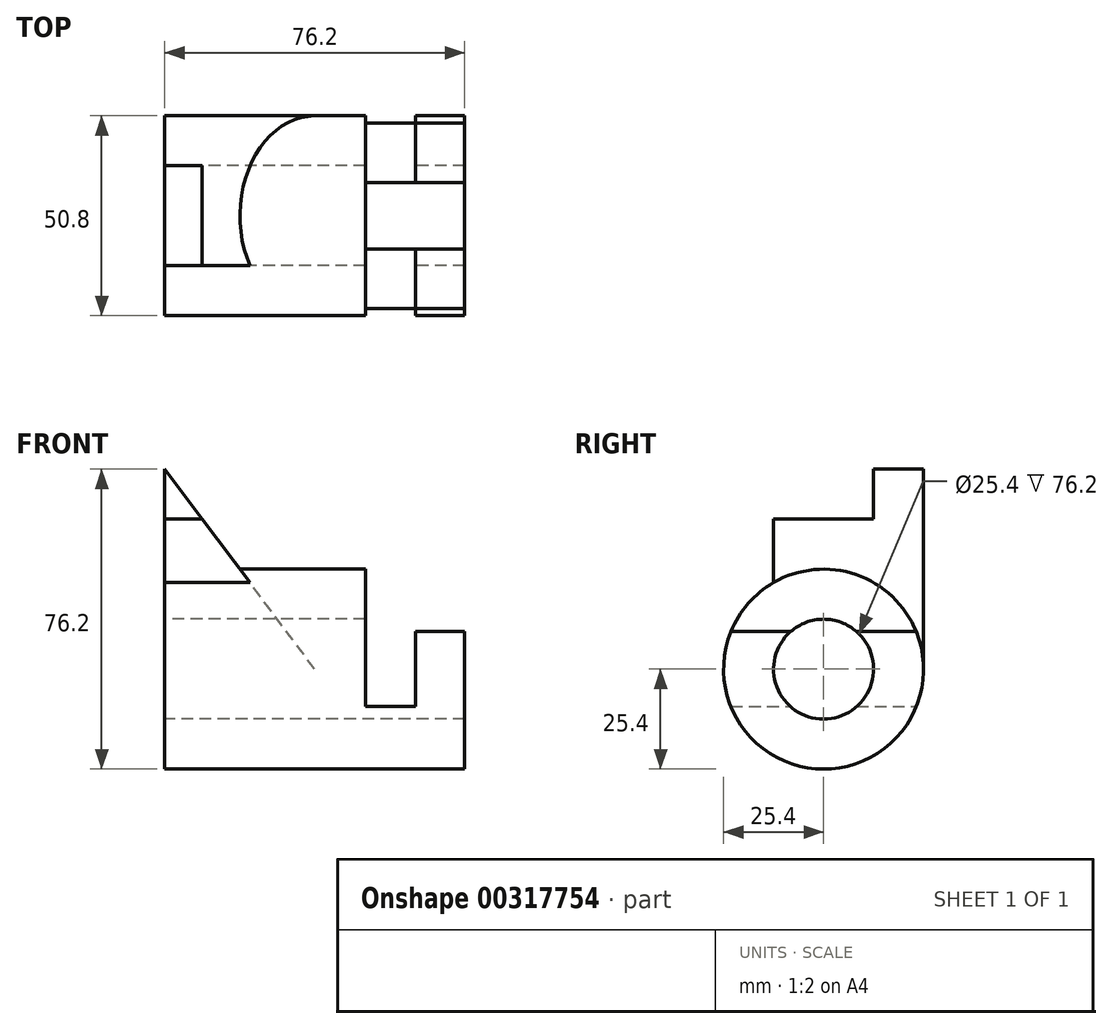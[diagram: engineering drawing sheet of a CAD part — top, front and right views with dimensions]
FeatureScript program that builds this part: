
annotation { "Feature Type Name" : "Feature", "Feature Type Description" : "" }
export const myFeature = defineFeature(function(context is Context, id is Id, definition is map)
    precondition{}
    {
        {
            var Q0;
            Q0=qCreatedBy(makeId("Front.planeOp"),FACE);
            var sketch = newSketch(context, id + "F0", { "sketchPlane" : qUnion([Q0])});
            skLineSegment(sketch, "E0", {"start": v(0, 0) * mm, "end": v(0, 50.8) * mm});
            skLineSegment(sketch, "E1", {"start": v(0, 0) * mm, "end": v(38.1, 0) * mm});
            skLineSegment(sketch, "E2", {"start": v(38.1, 0) * mm, "end": v(0, 50.8) * mm});
            skSolve(sketch);
        }
        {
            var Q0;
            Q0 = qSketchRegion(id + "F0", true);
            extrude(context, id + "F1", {"entities" : qUnion([Q0]), "oppositeDirection" : true, "depth" : 25.4 * mm});
        }
        {
            var Q0;
            Q0=makeQuery(id+"F1.opExtrude","CAP_FACE",FACE,{"disambiguationData":[OSD([sQuery(id+"F0.wireOp",EDGE,"E0"),sQuery(id+"F0.wireOp",EDGE,"E1"),sQuery(id+"F0.wireOp",EDGE,"E2")])],"isStart":true});
            var sketch = newSketch(context, id + "F2", { "sketchPlane" : qUnion([Q0])});
            skLineSegment(sketch, "E3", {"start": v(0, 50.8) * mm, "end": v(0, 0) * mm});
            skLineSegment(sketch, "E4", {"start": v(0, 0) * mm, "end": v(38.1, 0) * mm});
            skLineSegment(sketch, "E5", {"start": v(38.1, 0) * mm, "end": v(0, 50.8) * mm});
            skSolve(sketch);
        }
        {
            var Q0;
            Q0 = qSketchRegion(id + "F2", true);
            extrude(context, id + "F3", {"entities" : qUnion([Q0]), "operationType" : NewBodyOperationType.ADD, "depth" : 12.7 * mm});
        }
        {
            var Q0;
            Q0=makeQuery(id+"F3.boolean.opBoolean","MERGE",FACE,{"derivedFrom":[makeQuery(id+"F1.opExtrude","SWEPT_FACE",FACE,{"disambiguationData":[OSD([sQuery(id+"F0.wireOp",EDGE,"E0")])]}),makeQuery(id+"F3.opExtrude","SWEPT_FACE",FACE,{"disambiguationData":[OSD([sQuery(id+"F2.wireOp",EDGE,"E3")])]})]});
            var sketch = newSketch(context, id + "F4", { "sketchPlane" : qUnion([Q0])});
            skCircle(sketch, "E6", {"center": v(0, 0) * mm, "radius": 25.4 * mm});
            skSolve(sketch);
        }
        {
            var Q0;
            Q0 = qSketchRegion(id + "F4", true);
            extrude(context, id + "F5", {"entities" : qUnion([Q0]), "operationType" : NewBodyOperationType.ADD, "oppositeDirection" : true, "depth" : 76.2 * mm});
        }
        {
            var Q0;
            Q0=makeQuery(id+"F5.boolean.opBoolean","MERGE",FACE,{"derivedFrom":[makeQuery(id+"F3.boolean.opBoolean","MERGE",FACE,{"derivedFrom":[makeQuery(id+"F1.opExtrude","SWEPT_FACE",FACE,{"disambiguationData":[OSD([sQuery(id+"F0.wireOp",EDGE,"E0")])]}),makeQuery(id+"F3.opExtrude","SWEPT_FACE",FACE,{"disambiguationData":[OSD([sQuery(id+"F2.wireOp",EDGE,"E3")])]})]}),makeQuery(id+"F5.opExtrude","CAP_FACE",FACE,{"disambiguationData":[OSD([sQuery(id+"F4.wireOp",EDGE,"E6")])],"isStart":true})]});
            var sketch = newSketch(context, id + "F6", { "sketchPlane" : qUnion([Q0])});
            skCircle(sketch, "E7", {"center": v(0, 0) * mm, "radius": 12.7 * mm});
            skSolve(sketch);
        }
        {
            var Q0;
            Q0 = qSketchRegion(id + "F6", true);
            extrude(context, id + "F7", {"entities" : qUnion([Q0]), "operationType" : NewBodyOperationType.REMOVE, "endBound" : BoundingType.THROUGH_ALL, "oppositeDirection" : true, "depth" : 25.4 * mm});
        }
        {
            var Q0;
            Q0=makeQuery(id+"F5.boolean.opBoolean","MERGE",FACE,{"derivedFrom":[makeQuery(id+"F3.boolean.opBoolean","MERGE",FACE,{"derivedFrom":[makeQuery(id+"F1.opExtrude","SWEPT_FACE",FACE,{"disambiguationData":[OSD([sQuery(id+"F0.wireOp",EDGE,"E0")])]}),makeQuery(id+"F3.opExtrude","SWEPT_FACE",FACE,{"disambiguationData":[OSD([sQuery(id+"F2.wireOp",EDGE,"E3")])]})]}),makeQuery(id+"F5.opExtrude","CAP_FACE",FACE,{"disambiguationData":[OSD([sQuery(id+"F4.wireOp",EDGE,"E6")])],"isStart":true})]});
            var sketch = newSketch(context, id + "F8", { "sketchPlane" : qUnion([Q0])});
            skLineSegment(sketch, "E8.bottom", {"start": v(12.7, 50.8) * mm, "end": v(-12.7, 50.8) * mm});
            skLineSegment(sketch, "E8.top", {"start": v(12.7, 38.1) * mm, "end": v(-12.7, 38.1) * mm});
            skLineSegment(sketch, "E8.left", {"start": v(12.7, 50.8) * mm, "end": v(12.7, 38.1) * mm});
            skLineSegment(sketch, "E8.right", {"start": v(-12.7, 50.8) * mm, "end": v(-12.7, 38.1) * mm});
            skSolve(sketch);
        }
        {
            var Q0;
            Q0 = qSketchRegion(id + "F8", true);
            extrude(context, id + "F9", {"entities" : qUnion([Q0]), "operationType" : NewBodyOperationType.REMOVE, "endBound" : BoundingType.THROUGH_ALL, "oppositeDirection" : true, "depth" : 25.4 * mm});
        }
        {
            var Q0;
            Q0=makeQuery(id+"F1.opExtrude","CAP_FACE",FACE,{"disambiguationData":[OSD([sQuery(id+"F0.wireOp",EDGE,"E0"),sQuery(id+"F0.wireOp",EDGE,"E1"),sQuery(id+"F0.wireOp",EDGE,"E2")])],"isStart":false});
            var sketch = newSketch(context, id + "F10", { "sketchPlane" : qUnion([Q0])});
            skLineSegment(sketch, "E9", {"start": v(-76.35, 25.4) * mm, "end": v(-76.35, 9.53) * mm});
            skPoint(sketch, "E9.startSnap0", {"position": v(-19.05, 25.4) * mm});
            skLineSegment(sketch, "E10", {"start": v(-76.35, 9.53) * mm, "end": v(-63.65, 9.53) * mm});
            skLineSegment(sketch, "E11", {"start": v(-63.65, 9.53) * mm, "end": v(-63.65, -9.52) * mm});
            skLineSegment(sketch, "E12", {"start": v(-63.65, -9.52) * mm, "end": v(-50.95, -9.52) * mm});
            skLineSegment(sketch, "E13", {"start": v(-50.95, -9.52) * mm, "end": v(-50.95, 25.4) * mm});
            skLineSegment(sketch, "E14", {"start": v(-50.95, 25.4) * mm, "end": v(-76.35, 25.4) * mm});
            skSolve(sketch);
        }
        {
            var Q0;
            Q0 = qSketchRegion(id + "F10", true);
            extrude(context, id + "F11", {"entities" : qUnion([Q0]), "operationType" : NewBodyOperationType.REMOVE, "endBound" : BoundingType.THROUGH_ALL, "oppositeDirection" : true, "depth" : 25.4 * mm});
        }
    });
